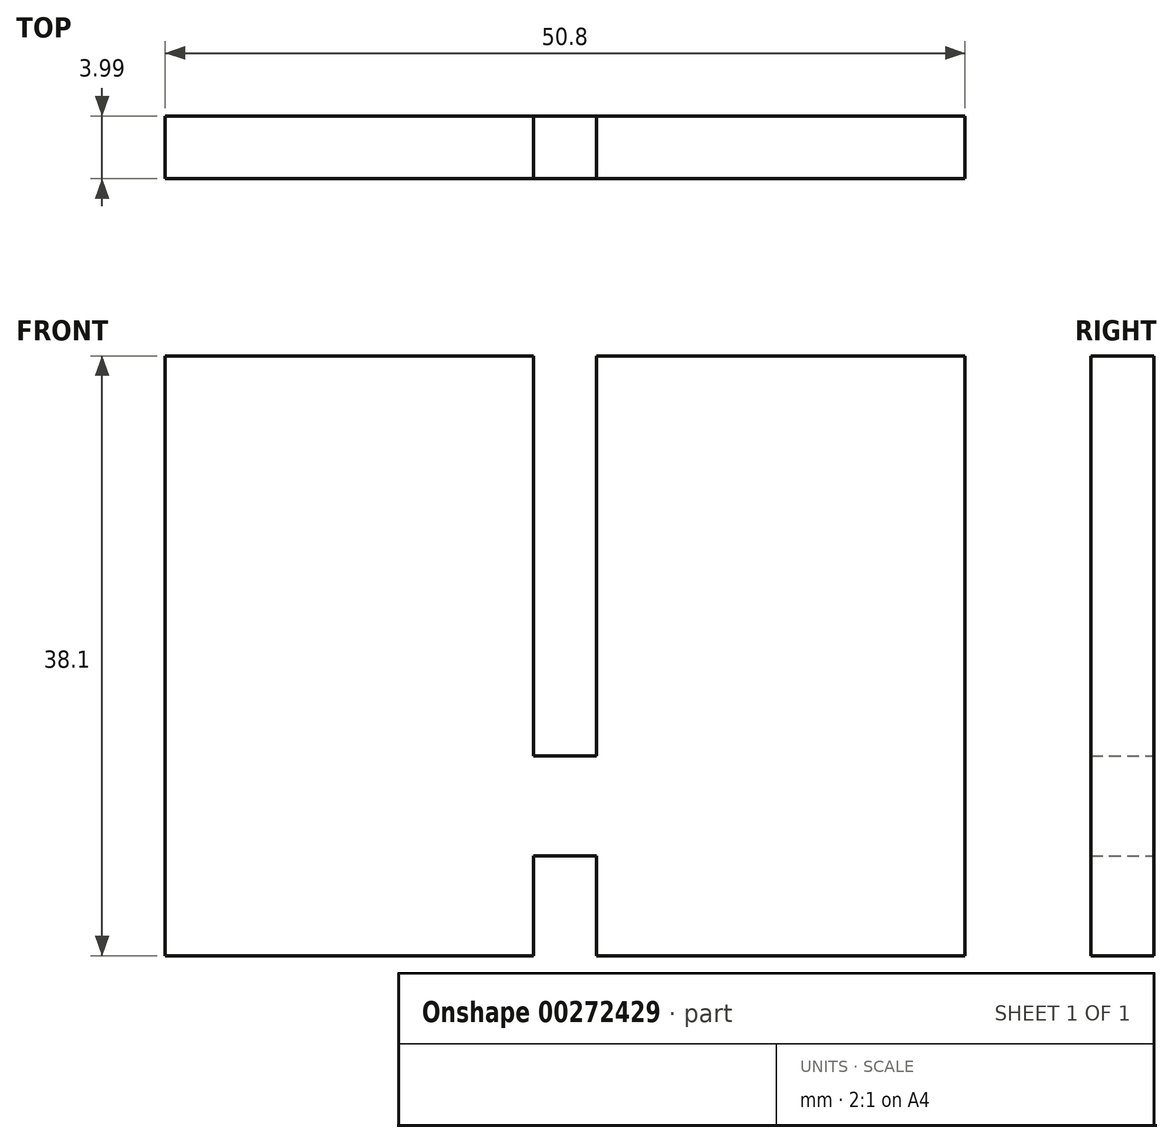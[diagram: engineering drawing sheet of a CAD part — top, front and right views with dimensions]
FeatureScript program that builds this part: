
annotation { "Feature Type Name" : "Feature", "Feature Type Description" : "" }
export const myFeature = defineFeature(function(context is Context, id is Id, definition is map)
    precondition{}
    {
        {
            var Q0;
            Q0=qCreatedBy(makeId("Front.planeOp"),FACE);
            var sketch = newSketch(context, id + "F0", { "sketchPlane" : qUnion([Q0])});
            skLineSegment(sketch, "E0", {"start": v(-2, 0) * mm, "end": v(-25.4, 0) * mm});
            skLineSegment(sketch, "E1", {"start": v(2, 0) * mm, "end": v(25.4, 0) * mm});
            skLineSegment(sketch, "E2", {"start": v(25.4, 0) * mm, "end": v(25.4, 38.1) * mm});
            skLineSegment(sketch, "E3", {"start": v(25.4, 38.1) * mm, "end": v(2, 38.1) * mm});
            skLineSegment(sketch, "E4", {"start": v(-25.4, 38.1) * mm, "end": v(-25.4, 0) * mm});
            skLineSegment(sketch, "E5", {"start": v(-2, 0) * mm, "end": v(-2, 6.35) * mm});
            skLineSegment(sketch, "E6", {"start": v(-2, 6.35) * mm, "end": v(2, 6.35) * mm});
            skLineSegment(sketch, "E7", {"start": v(2, 6.35) * mm, "end": v(2, 0) * mm});
            skLineSegment(sketch, "E8", {"start": v(2, 38.1) * mm, "end": v(2, 12.7) * mm});
            skLineSegment(sketch, "E9", {"start": v(2, 12.7) * mm, "end": v(-2, 12.7) * mm});
            skLineSegment(sketch, "E10", {"start": v(-2, 12.7) * mm, "end": v(-2, 38.1) * mm});
            skLineSegment(sketch, "E11.trimOffspring", {"start": v(-2, 38.1) * mm, "end": v(-25.4, 38.1) * mm});
            skPoint(sketch, "E12.orphan", {"position": v(0, 38.1) * mm});
            skSolve(sketch);
        }
        {
            var Q0;
            Q0 = qSketchRegion(id + "F0", true);
            extrude(context, id + "F1", {"entities" : qUnion([Q0]), "depth" : 4 * mm});
        }
    });
